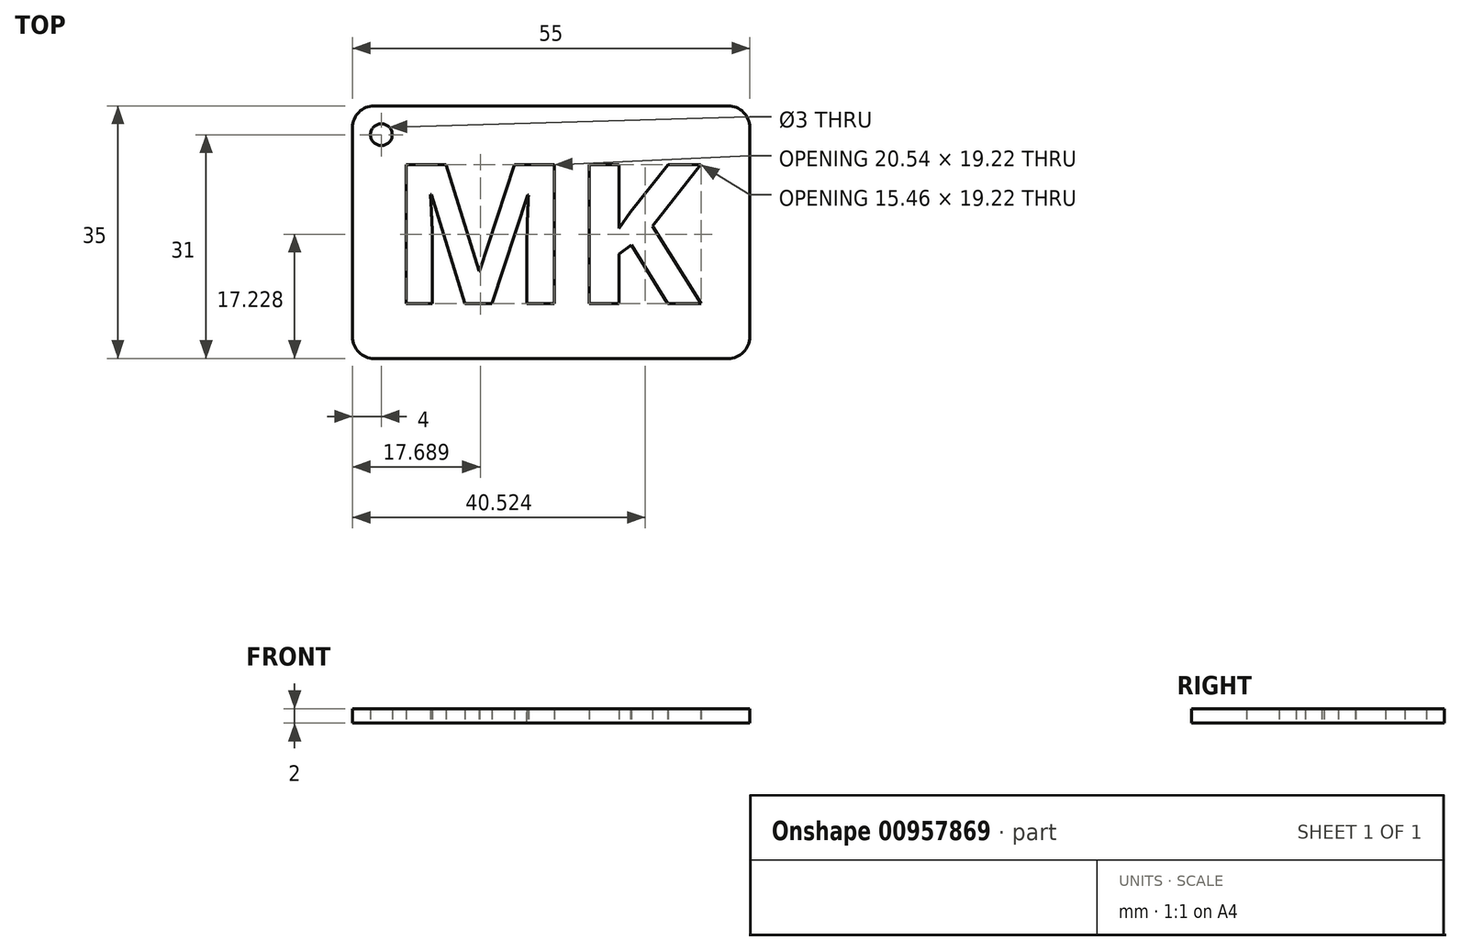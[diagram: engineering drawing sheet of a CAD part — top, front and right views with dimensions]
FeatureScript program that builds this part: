
annotation { "Feature Type Name" : "Feature", "Feature Type Description" : "" }
export const myFeature = defineFeature(function(context is Context, id is Id, definition is map)
    precondition{}
    {
        {
            var Q0;
            Q0=qCreatedBy(makeId("Top.planeOp"),FACE);
            var sketch = newSketch(context, id + "F0", { "sketchPlane" : qUnion([Q0])});
            skLineSegment(sketch, "E0.bottom", {"start": v(3, 0) * mm, "end": v(52, 0) * mm});
            skLineSegment(sketch, "E0.top", {"start": v(3, 35) * mm, "end": v(52, 35) * mm});
            skLineSegment(sketch, "E0.left", {"start": v(0, 3) * mm, "end": v(0, 32) * mm});
            skLineSegment(sketch, "E0.right", {"start": v(55, 3) * mm, "end": v(55, 32) * mm});
            skPoint(sketch, "E1.visualSharp", {"position": v(0, 35) * mm});
            skArc(sketch, "E1.filletArc", {"start": v(3, 35) * mm, "mid": v(0.88, 34.12) * mm, "end": v(0, 32) * mm});
            skPoint(sketch, "E2.visualSharp", {"position": v(55, 35) * mm});
            skArc(sketch, "E2.filletArc", {"start": v(55, 32) * mm, "mid": v(54.12, 34.12) * mm, "end": v(52, 35) * mm});
            skPoint(sketch, "E3.visualSharp", {"position": v(55, 0) * mm});
            skArc(sketch, "E3.filletArc", {"start": v(52, 0) * mm, "mid": v(54.12, 0.88) * mm, "end": v(55, 3) * mm});
            skPoint(sketch, "E4.visualSharp", {"position": v(0, 0) * mm});
            skArc(sketch, "E4.filletArc", {"start": v(0, 3) * mm, "mid": v(0.88, 0.88) * mm, "end": v(3, 0) * mm});
            skCircle(sketch, "E5", {"center": v(4, 31) * mm, "radius": 1.5 * mm});
            skText(sketch, "E6", { "text": "MK", "fontName": "OpenSans-Bold.ttf"});
            const initialGuessF0  = {"E6": [0.005, 0.00762, 1, 0, 0.01938]};
            skSetInitialGuess(sketch, initialGuessF0);
            skSolve(sketch);
        }
        {
            var Q0;
            Q0=makeQuery(id+"F0.imprint","IMPRINT",FACE,{"disambiguationData":[TD([[makeQuery(id+"F0.imprint","IMPRINT",EDGE,{"derivedFrom":sQuery(id+"F0.wireOp",EDGE,"E0.bottom")}),1.0]])]});
            extrude(context, id + "F1", {"entities" : qUnion([Q0]), "depth" : 2 * mm, "offsetDistance" : 25 * mm});
        }
    });
